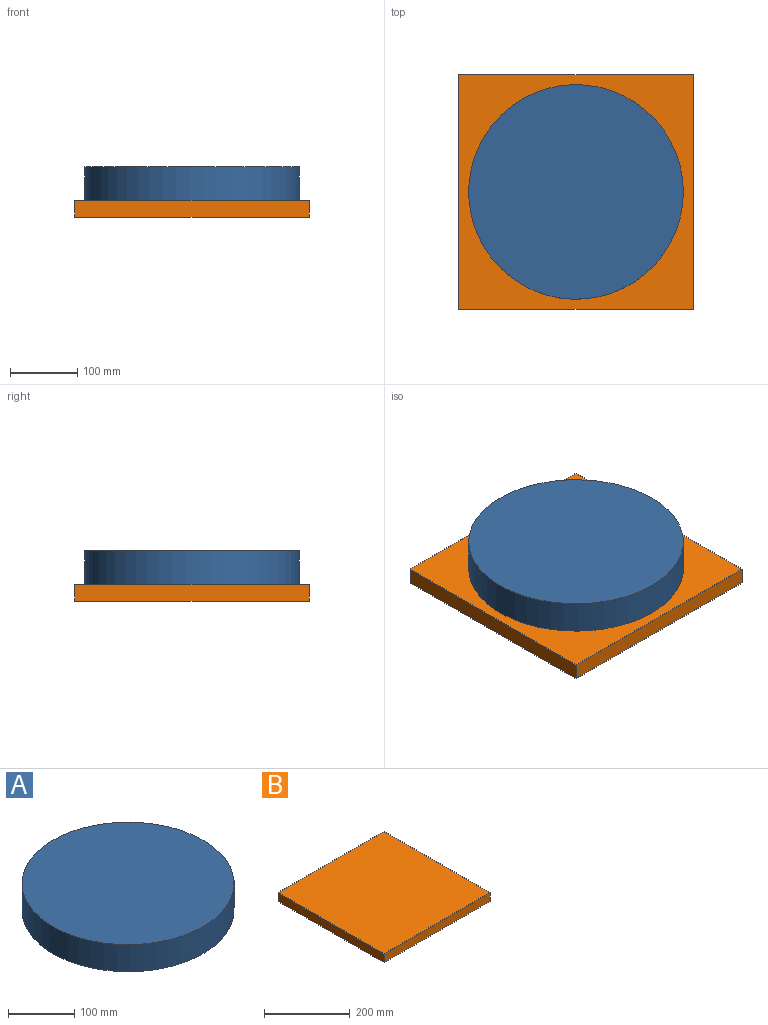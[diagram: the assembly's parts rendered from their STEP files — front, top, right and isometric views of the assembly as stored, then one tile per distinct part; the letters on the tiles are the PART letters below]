
ASSEMBLY  parts=2 mates=1
PART A: 3 faces, bbox 320x320x50 mm
  f0: cylinder r=160mm len=320mm, axis (0,0,-1), area 50265.5mm2, adj f1,f2
  f1: plane 320x320mm, normal (0,0,1), area 80424.8mm2, adj f0
  f2: plane 320x320mm, normal (0,0,-1), area 80424.8mm2, adj f0
PART B: 6 faces, bbox 350x350x25 mm
  f0: plane 350x25mm, normal (-1,0,0), area 8750mm2, adj f1,f3,f4,f5
  f1: plane 350x25mm, normal (0,-1,0), area 8750mm2, adj f0,f2,f4,f5
  f2: plane 350x25mm, normal (1,0,0), area 8750mm2, adj f1,f3,f4,f5
  f3: plane 350x25mm, normal (0,1,0), area 8750mm2, adj f0,f2,f4,f5
  f4: plane 350x350mm, normal (0,0,1), area 122500mm2, adj f0,f1,f2,f3
  f5: plane 350x350mm, normal (0,0,-1), area 122500mm2, adj f0,f1,f2,f3
PLACE A rot(axis=(0,0,1),0deg) t=(202.3,-642.47,25)mm
PLACE B at identity fixed
MATE planar A.f0 <-> B.f4  axis (0,0,-1) through (-530.19,134.68,25)mm
